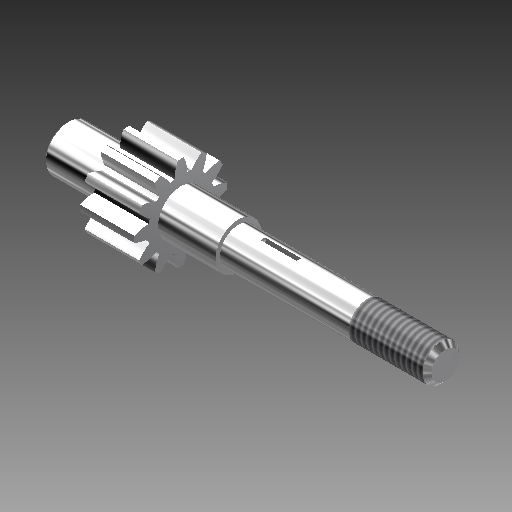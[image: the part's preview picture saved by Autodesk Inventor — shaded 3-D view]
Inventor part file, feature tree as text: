
AUTODESK INVENTOR PART (.ipt)
format: ipt  version: 2020 (Build 240168000, 168)  size: 228,352 bytes
history: native  units: in
note: dims shown in document units (in); Inventor stores cm internally (conversion verified against a paired STEP export)
features: other x3, chamfer x2, extrude x2, sketch x2, revolve x1, thread x1
ambient origin geometry x6: Origin, XZ Plane, XY Plane, X Axis, Y Axis, Z Axis
bodies: Solid1 (feature_tree)
feature tree (11):
  revolve  "Revolution1"  [1 undecoded]
  chamfer  "Chamfer1"  Distance=0.6238in
  chamfer  "Chamfer2"  Distance=0.5in
  thread  "Thread1"  [1 undecoded]
  extrude  "Extrusion1"  Depth=0.0625in TaperAngle=45.0deg
  extrude  "Extrusion2"  Depth=0.0625in TaperAngle=45.0deg
  other  "Start Plane"
  other  "Origin point"
  other  "Main Sketch"
  sketch  "Sketch3"  dims[d0=0.0in d1=0.0in d2=0.0in d3=0.6238in]
  sketch  "Sketch4"  dims[d4=0.892in d5=0.6238in d6=0.5in d7=0.0in d8=0.0312in d9=0.125in d10=45.0deg d11=0.0625in d12=0.125in d13=45.0deg d14=1.0in d15=0.0in d16=0.5757in d17=0.2486in d18=0.0625in d19=0.0in d20=1.0in d21=0.0in]
note: 2 required parameter values undecoded (feature->parameter linkage not recoverable at this tier; creation-order binding heuristic only, values carry confidence <= 0.55)